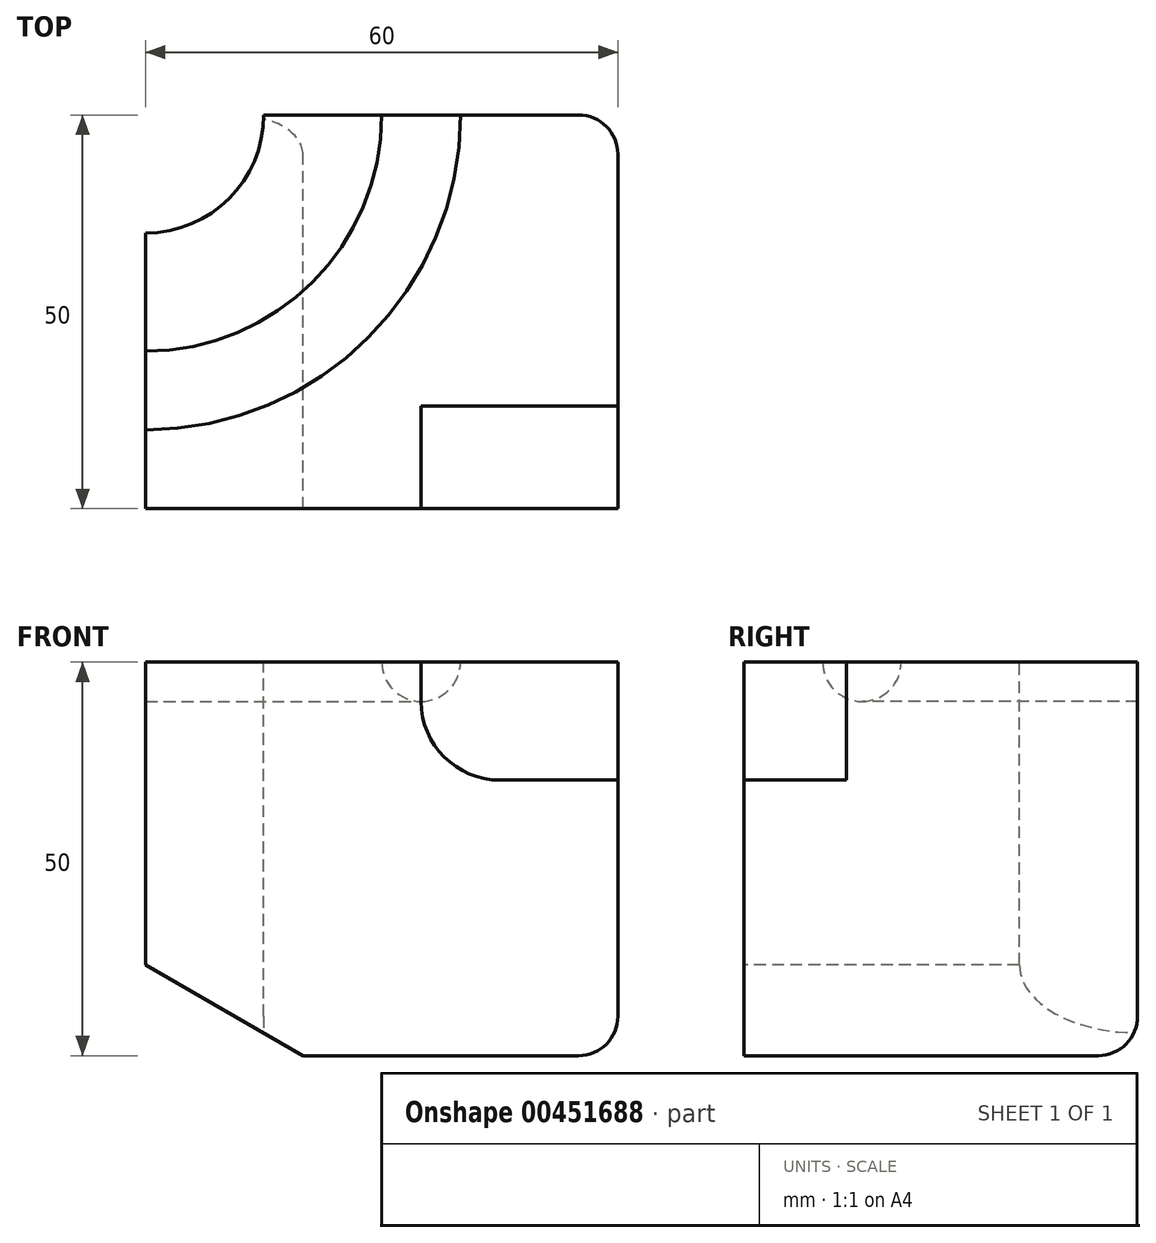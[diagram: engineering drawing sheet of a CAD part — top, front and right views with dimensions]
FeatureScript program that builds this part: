
annotation { "Feature Type Name" : "Feature", "Feature Type Description" : "" }
export const myFeature = defineFeature(function(context is Context, id is Id, definition is map)
    precondition{}
    {
        {
            var Q0;
            Q0=qCreatedBy(makeId("Top.planeOp"),FACE);
            var sketch = newSketch(context, id + "F0", { "sketchPlane" : qUnion([Q0])});
            skLineSegment(sketch, "E0.bottom", {"start": v(0, 0) * mm, "end": v(60, 0) * mm});
            skLineSegment(sketch, "E0.top", {"start": v(0, -50) * mm, "end": v(60, -50) * mm});
            skLineSegment(sketch, "E0.left", {"start": v(0, 0) * mm, "end": v(0, -50) * mm});
            skLineSegment(sketch, "E0.right", {"start": v(60, 0) * mm, "end": v(60, -50) * mm});
            skSolve(sketch);
        }
        {
            var Q0;
            Q0 = qSketchRegion(id + "F0", true);
            extrude(context, id + "F1", {"entities" : qUnion([Q0]), "depth" : 50 * mm});
        }
        {
            var Q0;
            Q0=qCreatedBy(makeId("Right.planeOp"),FACE);
            var sketch = newSketch(context, id + "F2", { "sketchPlane" : qUnion([Q0])});
            skLineSegment(sketch, "E1.bottom", {"start": v(0, 0) * mm, "end": v(-15, 0) * mm});
            skLineSegment(sketch, "E1.top", {"start": v(0, 50) * mm, "end": v(-15, 50) * mm});
            skLineSegment(sketch, "E1.left", {"start": v(0, 0) * mm, "end": v(0, 50) * mm});
            skLineSegment(sketch, "E1.right", {"start": v(-15, 0) * mm, "end": v(-15, 50) * mm});
            skArc(sketch, "E2", {"start": v(-40, 50) * mm, "mid": v(-35, 45) * mm, "end": v(-30, 50) * mm});
            skLineSegment(sketch, "E3", {"start": v(-30, 50) * mm, "end": v(-40, 50) * mm});
            skSolve(sketch);
        }
        {
            var Q0;
            Q0=makeQuery(id+"F2.imprint","IMPRINT",FACE,{"disambiguationData":[TD([[makeQuery(id+"F2.imprint","IMPRINT",EDGE,{"derivedFrom":sQuery(id+"F2.wireOp",EDGE,"E1.bottom")}),-1.0]])]});
            var Q1;
            Q1=makeQuery(id+"F2.imprint","IMPRINT",FACE,{"disambiguationData":[TD([[makeQuery(id+"F2.imprint","IMPRINT",EDGE,{"derivedFrom":sQuery(id+"F2.wireOp",EDGE,"E2")}),1.0]])]});
            var Q2;
            Q2=sQuery(id+"F2.wireOp",EDGE,"E1.left");
            revolve(context, id + "F3", {"operationType" : NewBodyOperationType.REMOVE, "entities" : qUnion([Q0, Q1]), "axis" : qUnion([Q2]), "revolveType" : RevolveType.FULL, "oppositeDirection" : true});
        }
        {
            var Q0;
            Q0=makeQuery(id+"F1.opExtrude","SWEPT_FACE",FACE,{"disambiguationData":[OSD([sQuery(id+"F0.wireOp",EDGE,"E0.top")])]});
            var sketch = newSketch(context, id + "F4", { "sketchPlane" : qUnion([Q0])});
            skLineSegment(sketch, "E4", {"start": v(35, 50) * mm, "end": v(60, 50) * mm});
            skLineSegment(sketch, "E5", {"start": v(60, 50) * mm, "end": v(60, 35) * mm});
            skLineSegment(sketch, "E6", {"start": v(60, 35) * mm, "end": v(45, 35) * mm});
            skArc(sketch, "E7", {"start": v(35, 45) * mm, "mid": v(37.93, 37.93) * mm, "end": v(45, 35) * mm});
            skLineSegment(sketch, "E8", {"start": v(35, 50) * mm, "end": v(35, 45) * mm});
            skSolve(sketch);
        }
        {
            var Q0;
            Q0 = qSketchRegion(id + "F4", true);
            extrude(context, id + "F5", {"entities" : qUnion([Q0]), "operationType" : NewBodyOperationType.REMOVE, "oppositeDirection" : true, "depth" : 13 * mm});
        }
        {
            var Q0;
            Q0=makeQuery(id+"F1.opExtrude","CAP_EDGE",EDGE,{"disambiguationData":[OSD([sQuery(id+"F0.wireOp",EDGE,"E0.left")])],"isStart":true});
            chamfer(context, id + "F6", {"entities" : qUnion([Q0]), "chamferType" : ChamferType.OFFSET_ANGLE, "width" : 20 * mm, "oppositeDirection" : true, "angle" : 30 * degree, "tangentPropagation" : true});
        }
        {
            var Q0;
            Q0=makeQuery(id+"F1.opExtrude","SWEPT_EDGE",EDGE,{"disambiguationData":[OSD([sQuery(id+"F0.wireOp",EDGE,"E0.bottom"),sQuery(id+"F0.wireOp",EDGE,"E0.right")])]});
            var Q1;
            Q1=makeQuery(id+"F1.opExtrude","CAP_EDGE",EDGE,{"disambiguationData":[OSD([sQuery(id+"F0.wireOp",EDGE,"E0.right")])],"isStart":true});
            var Q2;
            Q2=makeQuery(id+"F1.opExtrude","CAP_EDGE",EDGE,{"disambiguationData":[OSD([sQuery(id+"F0.wireOp",EDGE,"E0.bottom")])],"isStart":true});
            fillet(context, id + "F7", {"entities" : qUnion([Q0, Q1, Q2]), "radius" : 5 * mm, "tangentPropagation" : true, "allowEdgeOverflow" : false});
        }
    });
